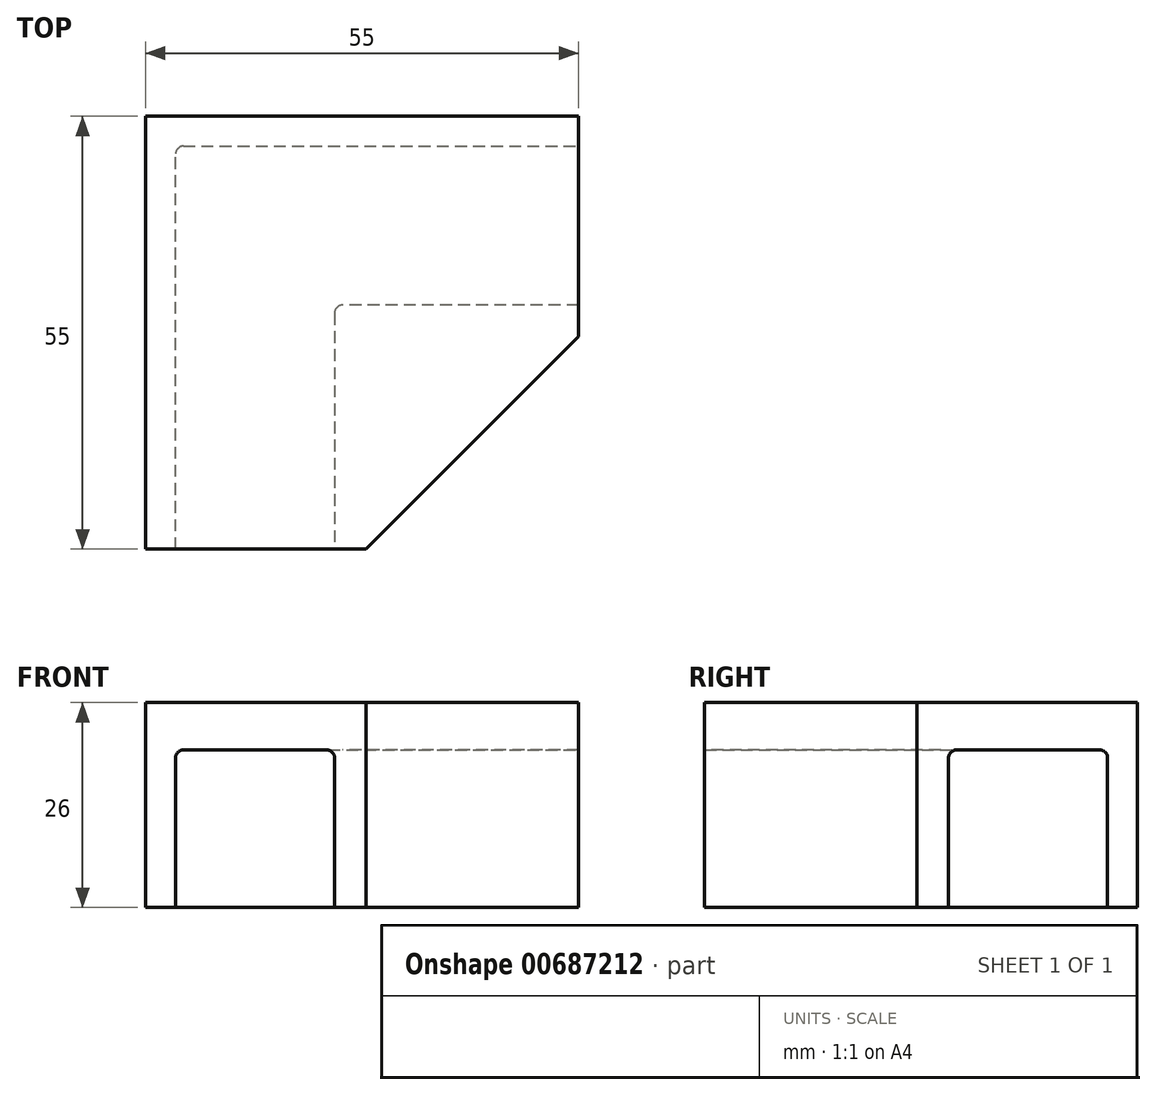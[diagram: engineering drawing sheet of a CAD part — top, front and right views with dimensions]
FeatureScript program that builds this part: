
annotation { "Feature Type Name" : "Feature", "Feature Type Description" : "" }
export const myFeature = defineFeature(function(context is Context, id is Id, definition is map)
    precondition{}
    {
        {
            var Q0;
            Q0=qCreatedBy(makeId("Top.planeOp"),FACE);
            var sketch = newSketch(context, id + "F0", { "sketchPlane" : qUnion([Q0])});
            skLineSegment(sketch, "E0", {"start": v(0, -55) * mm, "end": v(0, 0) * mm});
            skLineSegment(sketch, "E1", {"start": v(0, 0) * mm, "end": v(55, 0) * mm});
            skLineSegment(sketch, "E2", {"start": v(55, 0) * mm, "end": v(55, -28) * mm});
            skLineSegment(sketch, "E3", {"start": v(55, -28) * mm, "end": v(28, -28) * mm, "construction": true});
            skLineSegment(sketch, "E4", {"start": v(28, -28) * mm, "end": v(28, -55) * mm, "construction": true});
            skLineSegment(sketch, "E5", {"start": v(28, -55) * mm, "end": v(0, -55) * mm});
            skLineSegment(sketch, "E6", {"start": v(28, -55) * mm, "end": v(55, -28) * mm});
            skSolve(sketch);
        }
        {
            var Q0;
            Q0=makeQuery(id+"F0.imprint","IMPRINT",FACE,{"disambiguationData":[TD([[makeQuery(id+"F0.imprint","IMPRINT",EDGE,{"derivedFrom":sQuery(id+"F0.wireOp",EDGE,"E0")}),-1.0]])]});
            extrude(context, id + "F1", {"entities" : qUnion([Q0]), "oppositeDirection" : true, "depth" : 26 * mm, "offsetDistance" : 25 * mm});
        }
        {
            var Q0;
            Q0=makeQuery(id+"F1.opExtrude","CAP_FACE",FACE,{"disambiguationData":[OSD([sQuery(id+"F0.wireOp",EDGE,"E0"),sQuery(id+"F0.wireOp",EDGE,"E1"),sQuery(id+"F0.wireOp",EDGE,"E2"),sQuery(id+"F0.wireOp",EDGE,"E3"),sQuery(id+"F0.wireOp",EDGE,"E4"),sQuery(id+"F0.wireOp",EDGE,"E5")])],"isStart":false});
            var sketch = newSketch(context, id + "F2", { "sketchPlane" : qUnion([Q0])});
            skLineSegment(sketch, "E7", {"start": v(3.8, 55) * mm, "end": v(3.8, 3.8) * mm});
            skLineSegment(sketch, "E8", {"start": v(3.8, 3.8) * mm, "end": v(55, 3.8) * mm});
            skLineSegment(sketch, "E9", {"start": v(55, 3.8) * mm, "end": v(55, 24) * mm});
            skLineSegment(sketch, "E10", {"start": v(55, 24) * mm, "end": v(24, 24) * mm});
            skLineSegment(sketch, "E11", {"start": v(24, 24) * mm, "end": v(24, 55) * mm});
            skLineSegment(sketch, "E12", {"start": v(24, 55) * mm, "end": v(3.8, 55) * mm});
            skSolve(sketch);
        }
        {
            var Q0;
            Q0=makeQuery(id+"F2.imprint","IMPRINT",FACE,{"disambiguationData":[TD([[makeQuery(id+"F2.imprint","IMPRINT",EDGE,{"derivedFrom":sQuery(id+"F2.wireOp",EDGE,"E7")}),1.0]])]});
            extrude(context, id + "F3", {"entities" : qUnion([Q0]), "operationType" : NewBodyOperationType.REMOVE, "oppositeDirection" : true, "depth" : 20 * mm, "offsetDistance" : 25 * mm});
        }
        {
            var Q0;
            Q0=makeQuery(id+"F3.boolean.opBoolean","COPY",EDGE,{"derivedFrom":makeQuery(id+"F3.opExtrude","SWEPT_EDGE",EDGE,{"disambiguationData":[OSD([sQuery(id+"F2.wireOp",EDGE,"E7"),sQuery(id+"F2.wireOp",EDGE,"E8")])]})});
            var Q1;
            Q1=makeQuery(id+"F3.boolean.opBoolean","COPY",EDGE,{"derivedFrom":makeQuery(id+"F3.opExtrude","CAP_EDGE",EDGE,{"disambiguationData":[OSD([sQuery(id+"F2.wireOp",EDGE,"E7")])],"isStart":false})});
            var Q2;
            Q2=makeQuery(id+"F3.boolean.opBoolean","COPY",EDGE,{"derivedFrom":makeQuery(id+"F3.opExtrude","CAP_EDGE",EDGE,{"disambiguationData":[OSD([sQuery(id+"F2.wireOp",EDGE,"E8")])],"isStart":false})});
            var Q3;
            Q3=makeQuery(id+"F3.boolean.opBoolean","COPY",EDGE,{"derivedFrom":makeQuery(id+"F3.opExtrude","CAP_EDGE",EDGE,{"disambiguationData":[OSD([sQuery(id+"F2.wireOp",EDGE,"E11")])],"isStart":false})});
            var Q4;
            Q4=makeQuery(id+"F3.boolean.opBoolean","COPY",EDGE,{"derivedFrom":makeQuery(id+"F3.opExtrude","CAP_EDGE",EDGE,{"disambiguationData":[OSD([sQuery(id+"F2.wireOp",EDGE,"E10")])],"isStart":false})});
            var Q5;
            Q5=makeQuery(id+"F3.boolean.opBoolean","COPY",EDGE,{"derivedFrom":makeQuery(id+"F3.opExtrude","SWEPT_EDGE",EDGE,{"disambiguationData":[OSD([sQuery(id+"F2.wireOp",EDGE,"E10"),sQuery(id+"F2.wireOp",EDGE,"E11")])]})});
            fillet(context, id + "F4", {"entities" : qUnion([Q0, Q1, Q2, Q3, Q4, Q5]), "radius" : 1 * mm, "tangentPropagation" : true, "allowEdgeOverflow" : false});
        }
    });
